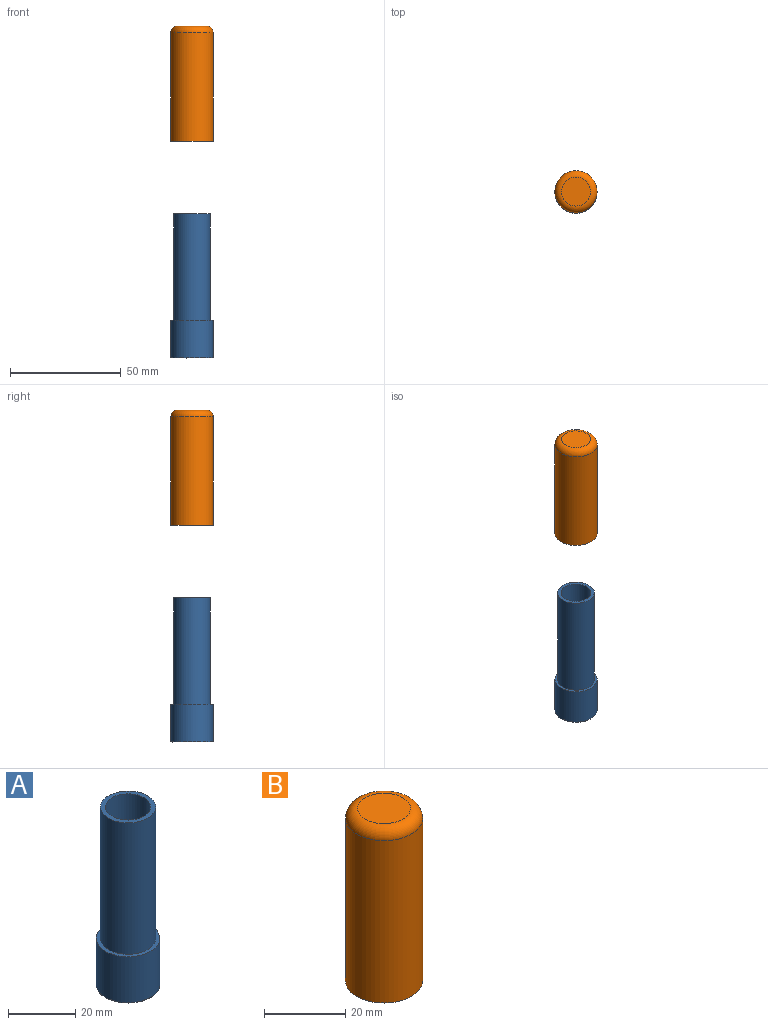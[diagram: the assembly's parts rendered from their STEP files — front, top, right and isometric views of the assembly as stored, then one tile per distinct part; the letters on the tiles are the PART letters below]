
ASSEMBLY  parts=2 mates=1
PART A: 12 faces, bbox 20.6x20.6x65 mm
  f0: cylinder r=9.5mm len=19mm, axis (0,0,-1), area 1002.8mm2, adj f2,f4
  f1: plane 18.6x18.6mm, normal (0,0,-1), area 80.6mm2, adj f2,f6
  f2: torus R=9.3mm, axis (0,0,1), area 18.6mm2, adj f0,f1
  f3: cylinder r=8.25mm len=48mm, axis (0,0,1), area 2488.1mm2, adj f4,f5
  f4: plane 19x19mm, normal (0,0,1), area 69.7mm2, adj f0,f3
  f5: plane 16.5x16.5mm, normal (0,0,1), area 70.7mm2, adj f3,f9
  f6: cylinder r=7.8mm len=15.6mm, axis (0,0,-1), area 78.4mm2, adj f1,f7
  f7: plane 15.6x15.6mm, normal (0,0,-1), area 191.1mm2, adj f6
  f8: cylinder r=8mm len=16mm, axis (0,0,-1), area 623.3mm2, adj f10,f11
  f9: cylinder r=6.75mm len=49.5mm, axis (0,0,1), area 2099.4mm2, adj f5,f10
  f10: plane 16x16mm, normal (0,0,-1), area 57.9mm2, adj f8,f9
  f11: plane 16x16mm, normal (0,0,1), area 201.1mm2, adj f8
PART B: 7 faces, bbox 20.6x20.6x52 mm
  f0: cylinder r=9.5mm len=49mm, axis (0,0,-1), area 2924.8mm2, adj f2,f3
  f1: plane 13x13mm, normal (0,0,1), area 132.7mm2, adj f3
  f2: plane 19x19mm, normal (0,0,-1), area 56.5mm2, adj f0,f4
  f3: torus R=6.5mm, axis (0,0,1), area 249mm2, adj f0,f1
  f4: cylinder r=8.5mm len=49mm, axis (0,0,-1), area 2616.9mm2, adj f2,f6
  f5: plane 13x13mm, normal (0,0,-1), area 132.7mm2, adj f6
  f6: torus R=6.5mm, axis (0,0,1), area 153.4mm2, adj f4,f5
PLACE A rot(axis=(-0.57,-0.13,-0.81),0deg) t=(-2.7,26.75,-117.76)mm
PLACE B rot(axis=(0,0,-1),90deg) t=(-2.7,26.75,-19.95)mm
MATE slider A.f0 <-> B.f0  axis (0,0,-1) through (-2.7,26.75,-117.76)mm
